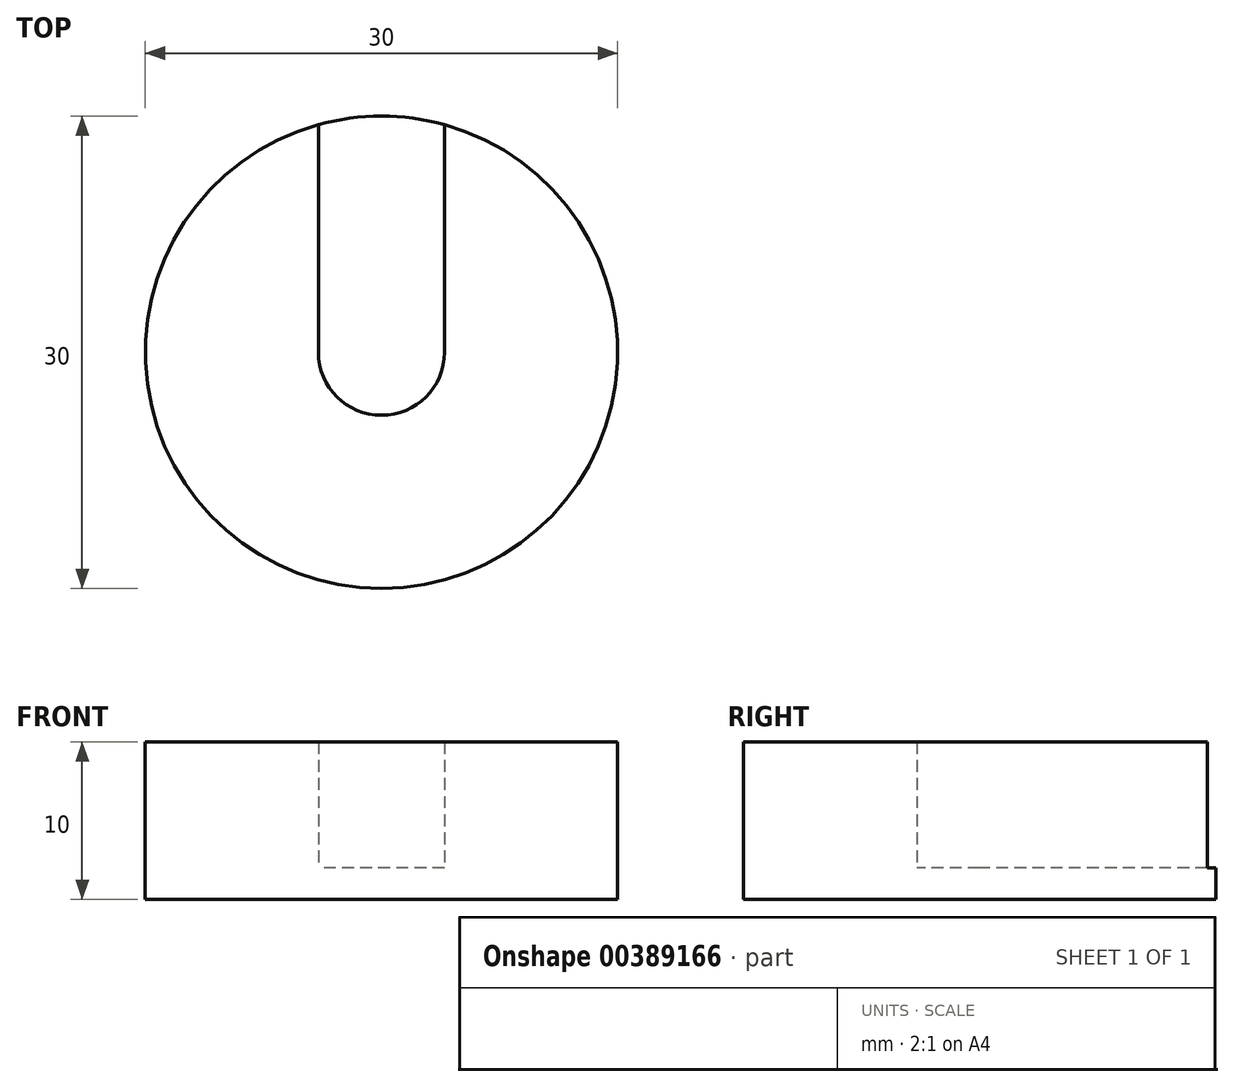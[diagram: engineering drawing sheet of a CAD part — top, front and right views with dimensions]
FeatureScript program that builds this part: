
annotation { "Feature Type Name" : "Feature", "Feature Type Description" : "" }
export const myFeature = defineFeature(function(context is Context, id is Id, definition is map)
    precondition{}
    {
        {
            var Q0;
            Q0=qCreatedBy(makeId("Top.planeOp"),FACE);
            var sketch = newSketch(context, id + "F0", { "sketchPlane" : qUnion([Q0])});
            skCircle(sketch, "E0", {"center": v(0, 0) * mm, "radius": 4 * mm});
            skCircle(sketch, "E1", {"center": v(0, 0) * mm, "radius": 15 * mm});
            skLineSegment(sketch, "E2", {"start": v(-4, 0) * mm, "end": v(-4, 14.46) * mm});
            skLineSegment(sketch, "E3", {"start": v(4, 0) * mm, "end": v(4, 14.46) * mm});
            skSolve(sketch);
        }
        {
            var Q0;
            {var subQ0=sQuery(id+"F0.wireOp",EDGE,"E2");Q0=makeQuery(id+"F0.imprint","IMPRINT",FACE,{"disambiguationData":[TD([[makeQuery(id+"F0.imprint","IMPRINT",EDGE,{"derivedFrom":subQ0}),1.0]])]});}
            var Q1;
            {var subQ0=sQuery(id+"F0.wireOp",EDGE,"E2");Q1=makeQuery(id+"F0.imprint","IMPRINT",FACE,{"disambiguationData":[TD([[makeQuery(id+"F0.imprint","IMPRINT",EDGE,{"derivedFrom":subQ0}),-1.0]])]});}
            var Q2;
            {var subQ0=sQuery(id+"F0.wireOp",EDGE,"E0");var subQ1=makeQuery(id+"F0.imprint","INTERSECT",VERTEX,{"derivedFrom":[subQ0,sQuery(id+"F0.wireOp",EDGE,"E2")]});Q2=makeQuery(id+"F0.imprint","IMPRINT",FACE,{"disambiguationData":[TD([[makeQuery(id+"F0.imprint","IMPRINT",EDGE,{"disambiguationData":[TD([[subQ1,1.0]])],"derivedFrom":subQ0}),1.0]])]});}
            extrude(context, id + "F1", {"entities" : qUnion([Q0, Q1, Q2]), "depth" : 2 * mm});
        }
        {
            var Q0;
            {var subQ0=sQuery(id+"F0.wireOp",EDGE,"E2");Q0=makeQuery(id+"F0.imprint","IMPRINT",FACE,{"disambiguationData":[TD([[makeQuery(id+"F0.imprint","IMPRINT",EDGE,{"derivedFrom":subQ0}),1.0]])]});}
            extrude(context, id + "F2", {"entities" : qUnion([Q0]), "operationType" : NewBodyOperationType.ADD, "depth" : 10 * mm});
        }
    });
